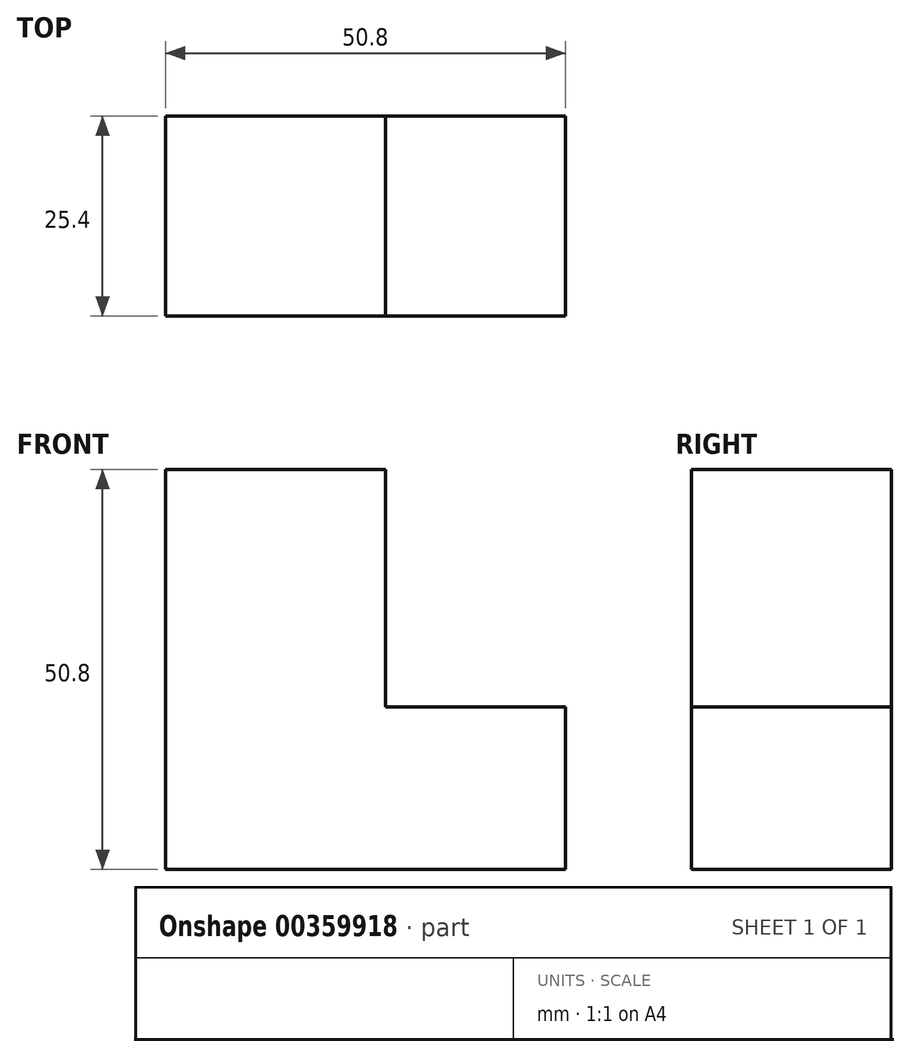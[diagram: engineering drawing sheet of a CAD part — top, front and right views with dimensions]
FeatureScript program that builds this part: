
annotation { "Feature Type Name" : "Feature", "Feature Type Description" : "" }
export const myFeature = defineFeature(function(context is Context, id is Id, definition is map)
    precondition{}
    {
        {
            var Q0;
            Q0=qCreatedBy(makeId("Front.planeOp"),FACE);
            var sketch = newSketch(context, id + "F0", { "sketchPlane" : qUnion([Q0])});
            skLineSegment(sketch, "E0", {"start": v(0, 0) * mm, "end": v(50.8, 0) * mm});
            skLineSegment(sketch, "E1", {"start": v(50.8, 0) * mm, "end": v(50.8, 14.53) * mm});
            skLineSegment(sketch, "E2", {"start": v(50.8, 14.53) * mm, "end": v(50.8, 20.62) * mm});
            skLineSegment(sketch, "E3", {"start": v(50.8, 20.62) * mm, "end": v(27.96, 20.62) * mm});
            skLineSegment(sketch, "E4", {"start": v(27.96, 20.62) * mm, "end": v(27.96, 50.8) * mm});
            skLineSegment(sketch, "E5", {"start": v(27.96, 50.8) * mm, "end": v(0, 50.8) * mm});
            skLineSegment(sketch, "E6", {"start": v(0, 50.8) * mm, "end": v(0, 0) * mm});
            skSolve(sketch);
        }
        {
            var Q0;
            Q0 = qSketchRegion(id + "F0", true);
            extrude(context, id + "F1", {"entities" : qUnion([Q0]), "depth" : 25.4 * mm});
        }
    });
